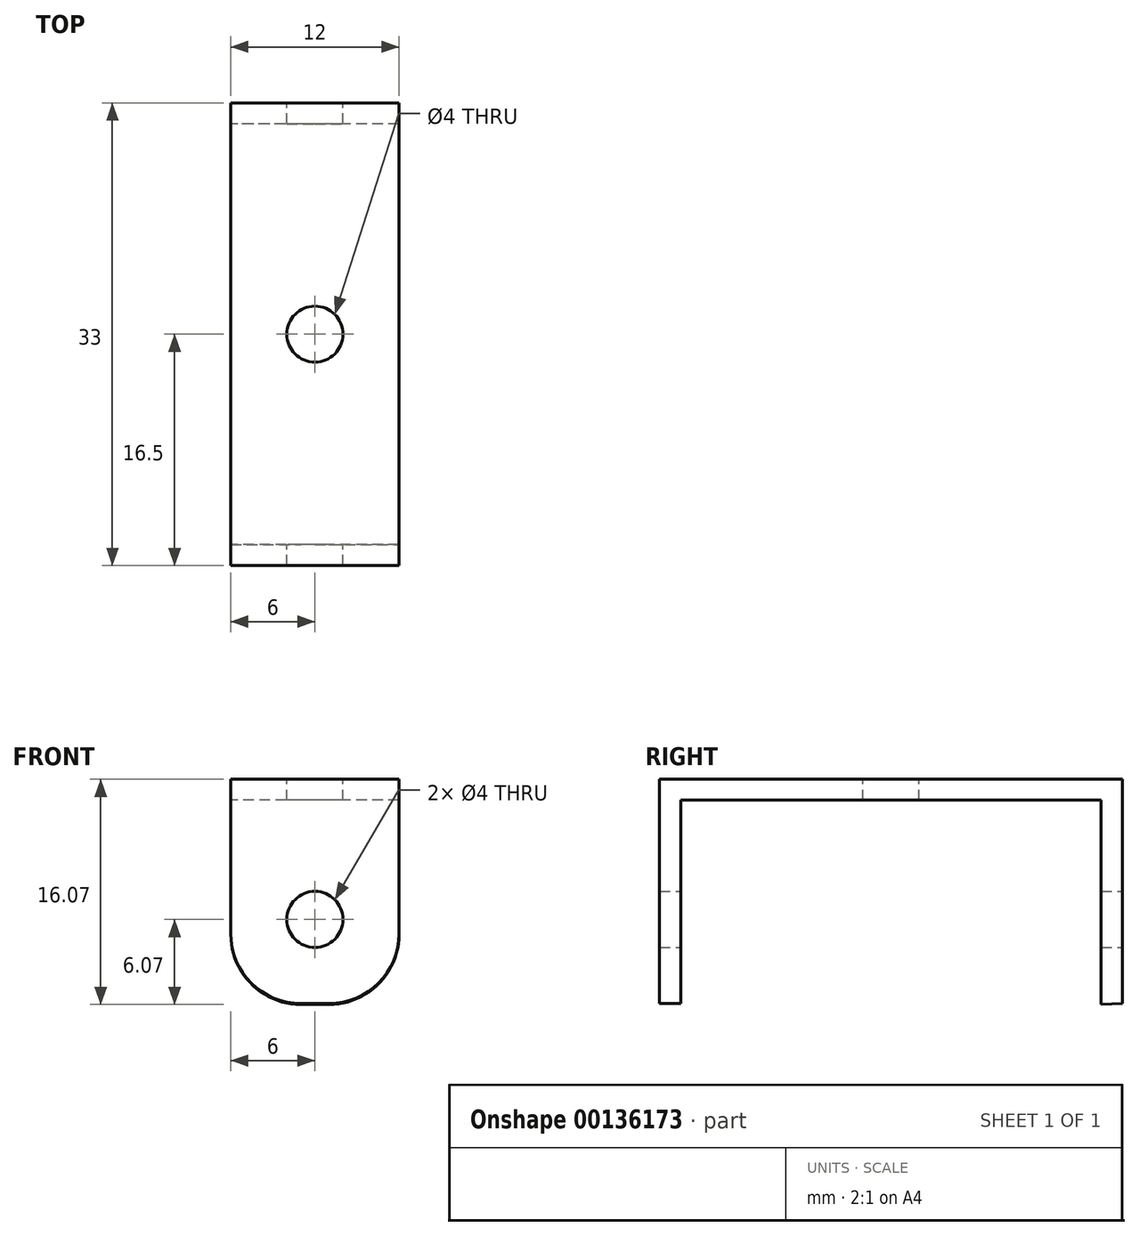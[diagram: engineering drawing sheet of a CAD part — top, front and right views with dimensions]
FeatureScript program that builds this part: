
annotation { "Feature Type Name" : "Feature", "Feature Type Description" : "" }
export const myFeature = defineFeature(function(context is Context, id is Id, definition is map)
    precondition{}
    {
        {
            var Q0;
            Q0=qCreatedBy(makeId("Right.planeOp"),FACE);
            var sketch = newSketch(context, id + "F0", { "sketchPlane" : qUnion([Q0])});
            skLineSegment(sketch, "E0", {"start": v(0, 0) * mm, "end": v(33, 0) * mm});
            skLineSegment(sketch, "E1", {"start": v(33, 0) * mm, "end": v(33, -16) * mm});
            skLineSegment(sketch, "E2", {"start": v(0, 0) * mm, "end": v(0, -16) * mm});
            skLineSegment(sketch, "E3", {"start": v(0, -16) * mm, "end": v(1.5, -16) * mm});
            skLineSegment(sketch, "E4", {"start": v(1.5, -16) * mm, "end": v(1.5, -1.5) * mm});
            skLineSegment(sketch, "E5", {"start": v(1.5, -1.5) * mm, "end": v(31.5, -1.5) * mm});
            skLineSegment(sketch, "E6", {"start": v(31.5, -1.5) * mm, "end": v(31.5, -16.07) * mm});
            skLineSegment(sketch, "E7", {"start": v(31.5, -16.07) * mm, "end": v(33, -16) * mm});
            skSolve(sketch);
        }
        {
            var Q0;
            Q0 = qSketchRegion(id + "F0", true);
            extrude(context, id + "F1", {"entities" : qUnion([Q0]), "depth" : 12 * mm});
        }
        {
            var Q0;
            Q0=makeQuery(id+"F1.opExtrude","SWEPT_FACE",FACE,{"disambiguationData":[OSD([sQuery(id+"F0.wireOp",EDGE,"E0")])]});
            var sketch = newSketch(context, id + "F2", { "sketchPlane" : qUnion([Q0])});
            skCircle(sketch, "E8", {"center": v(6, 16.5) * mm, "radius": 2 * mm});
            skSolve(sketch);
        }
        {
            var Q0;
            Q0 = qSketchRegion(id + "F2", true);
            extrude(context, id + "F3", {"entities" : qUnion([Q0]), "operationType" : NewBodyOperationType.REMOVE, "oppositeDirection" : true, "depth" : 25 * mm});
        }
        {
            var Q0;
            Q0=makeQuery(id+"F1.opExtrude","SWEPT_FACE",FACE,{"disambiguationData":[OSD([sQuery(id+"F0.wireOp",EDGE,"E1")])]});
            var sketch = newSketch(context, id + "F4", { "sketchPlane" : qUnion([Q0])});
            skCircle(sketch, "E9", {"center": v(-6, -10) * mm, "radius": 2 * mm});
            skSolve(sketch);
        }
        {
            var Q0;
            Q0=makeQuery(id+"F4.imprint","IMPRINT",FACE,{"disambiguationData":[TD([[makeQuery(id+"F4.imprint","IMPRINT",EDGE,{"derivedFrom":sQuery(id+"F4.wireOp",EDGE,"E9")}),1.0]])]});
            extrude(context, id + "F5", {"entities" : qUnion([Q0]), "operationType" : NewBodyOperationType.REMOVE, "oppositeDirection" : true, "depth" : 45 * mm});
        }
        {
            var Q0;
            Q0=makeQuery(id+"F1.opExtrude","CAP_EDGE",EDGE,{"disambiguationData":[OSD([sQuery(id+"F0.wireOp",EDGE,"E7")])],"isStart":true});
            var Q1;
            Q1=makeQuery(id+"F1.opExtrude","CAP_EDGE",EDGE,{"disambiguationData":[OSD([sQuery(id+"F0.wireOp",EDGE,"E7")])],"isStart":false});
            var Q2;
            Q2=makeQuery(id+"F1.opExtrude","CAP_EDGE",EDGE,{"disambiguationData":[OSD([sQuery(id+"F0.wireOp",EDGE,"E3")])],"isStart":false});
            var Q3;
            Q3=makeQuery(id+"F1.opExtrude","CAP_EDGE",EDGE,{"disambiguationData":[OSD([sQuery(id+"F0.wireOp",EDGE,"E3")])],"isStart":true});
            fillet(context, id + "F6", {"entities" : qUnion([Q0, Q1, Q2, Q3]), "radius" : 5 * mm, "tangentPropagation" : true, "allowEdgeOverflow" : false});
        }
    });
